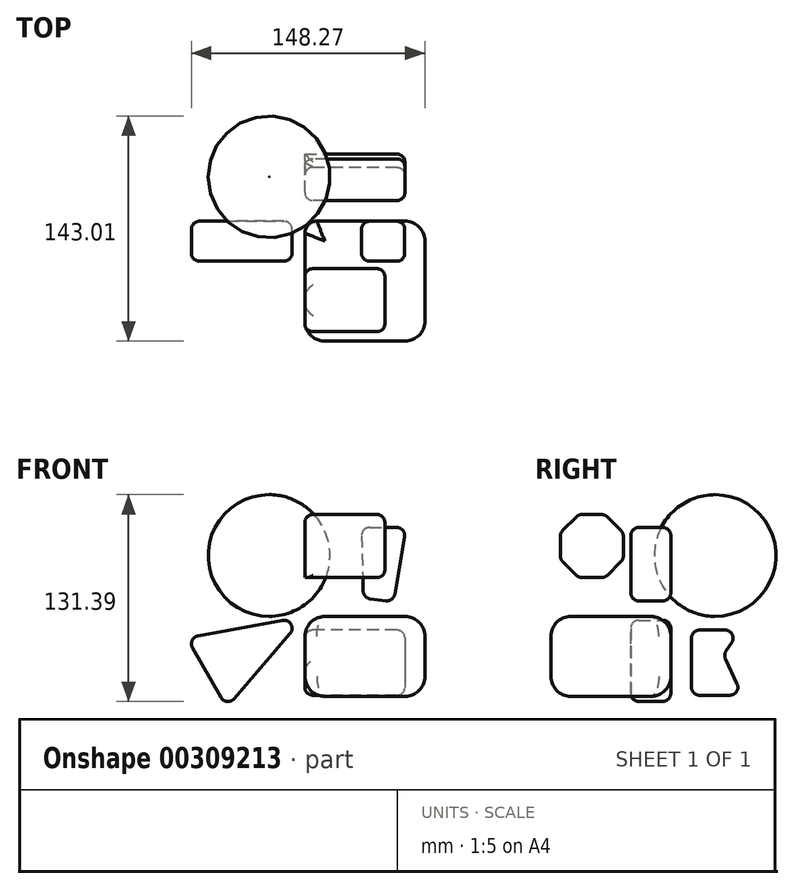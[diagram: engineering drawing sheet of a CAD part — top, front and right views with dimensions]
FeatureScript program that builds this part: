
annotation { "Feature Type Name" : "Feature", "Feature Type Description" : "" }
export const myFeature = defineFeature(function(context is Context, id is Id, definition is map)
    precondition{}
    {
        {
            var Q0;
            Q0=qCreatedBy(makeId("Top.planeOp"),FACE);
            var sketch = newSketch(context, id + "F0", { "sketchPlane" : qUnion([Q0])});
            skCircle(sketch, "E0", {"center": v(-22.77, 28.16) * mm, "radius": 38.66 * mm});
            skSolve(sketch);
        }
        {
            var Q0;
            Q0 = qSketchRegion(id + "F0", true);
            extrude(context, id + "F1", {"entities" : qUnion([Q0]), "depth" : 77.32 * mm});
        }
        {
            var Q0;
            Q0=makeQuery(id+"F1.opExtrude","CAP_EDGE",EDGE,{"disambiguationData":[OSD([sQuery(id+"F0.wireOp",EDGE,"E0")])],"isStart":false});
            var Q1;
            Q1=makeQuery(id+"F1.opExtrude","CAP_EDGE",EDGE,{"disambiguationData":[OSD([sQuery(id+"F0.wireOp",EDGE,"E0")])],"isStart":true});
            fillet(context, id + "F2", {"entities" : qUnion([Q0, Q1]), "radius" : 38.66 * mm, "tangentPropagation" : true, "allowEdgeOverflow" : false});
        }
        {
            var Q0;
            Q0=qCreatedBy(makeId("Front.planeOp"),FACE);
            var sketch = newSketch(context, id + "F3", { "sketchPlane" : qUnion([Q0])});
            skLineSegment(sketch, "E1", {"start": v(0, 0) * mm, "end": v(0, -50.8) * mm});
            skLineSegment(sketch, "E2", {"start": v(0, -50.8) * mm, "end": v(76.2, -50.8) * mm});
            skLineSegment(sketch, "E3", {"start": v(0, 0) * mm, "end": v(76.2, 0) * mm});
            skLineSegment(sketch, "E4", {"start": v(76.2, 0) * mm, "end": v(76.2, -50.8) * mm});
            skSolve(sketch);
        }
        {
            var Q0;
            Q0=makeQuery(id+"F3.imprint","IMPRINT",FACE,{"disambiguationData":[TD([[makeQuery(id+"F3.imprint","IMPRINT",EDGE,{"derivedFrom":sQuery(id+"F3.wireOp",EDGE,"E1")}),1.0]])]});
            extrude(context, id + "F4", {"entities" : qUnion([Q0]), "depth" : 76.2 * mm});
        }
        {
            var Q0;
            Q0=makeQuery(id+"F4.opExtrude","SWEPT_FACE",FACE,{"disambiguationData":[OSD([sQuery(id+"F3.wireOp",EDGE,"E4")])]});
            var Q1;
            Q1=makeQuery(id+"F4.opExtrude","CAP_FACE",FACE,{"disambiguationData":[OSD([sQuery(id+"F3.wireOp",EDGE,"E1"),sQuery(id+"F3.wireOp",EDGE,"E2"),sQuery(id+"F3.wireOp",EDGE,"E3"),sQuery(id+"F3.wireOp",EDGE,"E4")])],"isStart":false});
            var Q2;
            Q2=makeQuery(id+"F4.opExtrude","SWEPT_EDGE",EDGE,{"disambiguationData":[OSD([sQuery(id+"F3.wireOp",EDGE,"E1"),sQuery(id+"F3.wireOp",EDGE,"E3")])]});
            var Q3;
            Q3=makeQuery(id+"F4.opExtrude","CAP_EDGE",EDGE,{"disambiguationData":[OSD([sQuery(id+"F3.wireOp",EDGE,"E3")])],"isStart":true});
            var Q4;
            Q4=makeQuery(id+"F4.opExtrude","CAP_EDGE",EDGE,{"disambiguationData":[OSD([sQuery(id+"F3.wireOp",EDGE,"E2")])],"isStart":true});
            var Q5;
            Q5=makeQuery(id+"F4.opExtrude","SWEPT_EDGE",EDGE,{"disambiguationData":[OSD([sQuery(id+"F3.wireOp",EDGE,"E1"),sQuery(id+"F3.wireOp",EDGE,"E2")])]});
            fillet(context, id + "F5", {"entities" : qUnion([Q0, Q1, Q2, Q3, Q4, Q5]), "radius" : 12.7 * mm, "tangentPropagation" : true, "allowEdgeOverflow" : false});
        }
        {
            var Q0;
            Q0=makeQuery(id+"F4.opExtrude","CAP_EDGE",EDGE,{"disambiguationData":[OSD([sQuery(id+"F3.wireOp",EDGE,"E1")])],"isStart":true});
            fillet(context, id + "F6", {"entities" : qUnion([Q0]), "radius" : 7.62 * mm, "tangentPropagation" : true, "allowEdgeOverflow" : false});
        }
        {
            var Q0;
            Q0=qCreatedBy(makeId("Front.planeOp"),FACE);
            var sketch = newSketch(context, id + "F7", { "sketchPlane" : qUnion([Q0])});
            skLineSegment(sketch, "E5", {"start": v(0, 0) * mm, "end": v(-49.72, -57.75) * mm});
            skLineSegment(sketch, "E6", {"start": v(-49.72, -57.75) * mm, "end": v(-74.96, -13.67) * mm});
            skLineSegment(sketch, "E7", {"start": v(-74.96, -13.67) * mm, "end": v(0, 0) * mm});
            skSolve(sketch);
        }
        {
            var Q0;
            Q0=makeQuery(id+"F7.imprint","IMPRINT",FACE,{"disambiguationData":[TD([[makeQuery(id+"F7.imprint","IMPRINT",EDGE,{"derivedFrom":sQuery(id+"F7.wireOp",EDGE,"E5")}),-1.0]])]});
            extrude(context, id + "F8", {"entities" : qUnion([Q0]), "depth" : 25.4 * mm});
        }
        {
            var Q0;
            Q0=makeQuery(id+"F8.opExtrude","CAP_EDGE",EDGE,{"disambiguationData":[OSD([sQuery(id+"F7.wireOp",EDGE,"E7")])],"isStart":false});
            var Q1;
            Q1=makeQuery(id+"F8.opExtrude","CAP_EDGE",EDGE,{"disambiguationData":[OSD([sQuery(id+"F7.wireOp",EDGE,"E6")])],"isStart":false});
            var Q2;
            Q2=makeQuery(id+"F8.opExtrude","CAP_EDGE",EDGE,{"disambiguationData":[OSD([sQuery(id+"F7.wireOp",EDGE,"E5")])],"isStart":false});
            var Q3;
            Q3=makeQuery(id+"F8.opExtrude","CAP_EDGE",EDGE,{"disambiguationData":[OSD([sQuery(id+"F7.wireOp",EDGE,"E5")])],"isStart":true});
            var Q4;
            Q4=makeQuery(id+"F8.opExtrude","CAP_EDGE",EDGE,{"disambiguationData":[OSD([sQuery(id+"F7.wireOp",EDGE,"E6")])],"isStart":true});
            var Q5;
            Q5=makeQuery(id+"F8.opExtrude","SWEPT_EDGE",EDGE,{"disambiguationData":[OSD([sQuery(id+"F7.wireOp",EDGE,"E5"),sQuery(id+"F7.wireOp",EDGE,"E6")])]});
            var Q6;
            Q6=makeQuery(id+"F8.opExtrude","SWEPT_EDGE",EDGE,{"disambiguationData":[OSD([sQuery(id+"F7.wireOp",EDGE,"E6"),sQuery(id+"F7.wireOp",EDGE,"E7")])]});
            var Q7;
            Q7=makeQuery(id+"F8.opExtrude","CAP_EDGE",EDGE,{"disambiguationData":[OSD([sQuery(id+"F7.wireOp",EDGE,"E7")])],"isStart":true});
            var Q8;
            Q8=makeQuery(id+"F8.opExtrude","SWEPT_EDGE",EDGE,{"disambiguationData":[OSD([sQuery(id+"F7.wireOp",EDGE,"E5"),sQuery(id+"F7.wireOp",EDGE,"E7")])]});
            fillet(context, id + "F9", {"entities" : qUnion([Q0, Q1, Q2, Q3, Q4, Q5, Q6, Q7, Q8]), "radius" : 5.08 * mm, "tangentPropagation" : true, "allowEdgeOverflow" : false});
        }
        {
            var Q0;
            Q0=qCreatedBy(makeId("Right.planeOp"),FACE);
            var sketch = newSketch(context, id + "F10", { "sketchPlane" : qUnion([Q0])});
            skLineSegment(sketch, "E8", {"start": v(13.1, -8.7) * mm, "end": v(13.1, -50.08) * mm});
            skLineSegment(sketch, "E9", {"start": v(13.1, -8.7) * mm, "end": v(44, -8.7) * mm});
            skLineSegment(sketch, "E10", {"start": v(44, -8.7) * mm, "end": v(33.51, -24.43) * mm});
            skLineSegment(sketch, "E11", {"start": v(13.1, -50.08) * mm, "end": v(45.5, -50.08) * mm});
            skLineSegment(sketch, "E12", {"start": v(33.51, -24.43) * mm, "end": v(45.5, -50.08) * mm});
            skSolve(sketch);
        }
        {
            var Q0;
            Q0=makeQuery(id+"F10.imprint","IMPRINT",FACE,{"disambiguationData":[TD([[makeQuery(id+"F10.imprint","IMPRINT",EDGE,{"derivedFrom":sQuery(id+"F10.wireOp",EDGE,"E8")}),1.0]])]});
            extrude(context, id + "F11", {"entities" : qUnion([Q0]), "depth" : 63.5 * mm});
        }
        {
            var Q0;
            Q0=makeQuery(id+"F11.opExtrude","CAP_EDGE",EDGE,{"disambiguationData":[OSD([sQuery(id+"F10.wireOp",EDGE,"E9")])],"isStart":false});
            var Q1;
            Q1=makeQuery(id+"F11.opExtrude","CAP_EDGE",EDGE,{"disambiguationData":[OSD([sQuery(id+"F10.wireOp",EDGE,"E8")])],"isStart":false});
            var Q2;
            Q2=makeQuery(id+"F11.opExtrude","CAP_EDGE",EDGE,{"disambiguationData":[OSD([sQuery(id+"F10.wireOp",EDGE,"E11")])],"isStart":false});
            var Q3;
            Q3=makeQuery(id+"F11.opExtrude","CAP_EDGE",EDGE,{"disambiguationData":[OSD([sQuery(id+"F10.wireOp",EDGE,"E12")])],"isStart":false});
            var Q4;
            Q4=makeQuery(id+"F11.opExtrude","CAP_EDGE",EDGE,{"disambiguationData":[OSD([sQuery(id+"F10.wireOp",EDGE,"E10")])],"isStart":false});
            var Q5;
            Q5=makeQuery(id+"F11.opExtrude","SWEPT_EDGE",EDGE,{"disambiguationData":[OSD([sQuery(id+"F10.wireOp",EDGE,"E9"),sQuery(id+"F10.wireOp",EDGE,"E10")])]});
            var Q6;
            Q6=makeQuery(id+"F11.opExtrude","SWEPT_FACE",FACE,{"disambiguationData":[OSD([sQuery(id+"F10.wireOp",EDGE,"E10")])]});
            var Q7;
            Q7=makeQuery(id+"F11.opExtrude","SWEPT_EDGE",EDGE,{"disambiguationData":[OSD([sQuery(id+"F10.wireOp",EDGE,"E11"),sQuery(id+"F10.wireOp",EDGE,"E12")])]});
            var Q8;
            Q8=makeQuery(id+"F11.opExtrude","SWEPT_FACE",FACE,{"disambiguationData":[OSD([sQuery(id+"F10.wireOp",EDGE,"E9")])]});
            var Q9;
            Q9=makeQuery(id+"F11.opExtrude","CAP_EDGE",EDGE,{"disambiguationData":[OSD([sQuery(id+"F10.wireOp",EDGE,"E8")])],"isStart":true});
            var Q10;
            Q10=makeQuery(id+"F11.opExtrude","SWEPT_EDGE",EDGE,{"disambiguationData":[OSD([sQuery(id+"F10.wireOp",EDGE,"E8"),sQuery(id+"F10.wireOp",EDGE,"E11")])]});
            var Q11;
            Q11=makeQuery(id+"F11.opExtrude","CAP_EDGE",EDGE,{"disambiguationData":[OSD([sQuery(id+"F10.wireOp",EDGE,"E11")])],"isStart":true});
            fillet(context, id + "F12", {"entities" : qUnion([Q0, Q1, Q2, Q3, Q4, Q5, Q6, Q7, Q8, Q9, Q10, Q11]), "radius" : 5.08 * mm, "tangentPropagation" : true, "allowEdgeOverflow" : false});
        }
        {
            var Q0;
            Q0=qCreatedBy(makeId("Front.planeOp"),FACE);
            var sketch = newSketch(context, id + "F13", { "sketchPlane" : qUnion([Q0])});
            skLineSegment(sketch, "E13", {"start": v(35.85, 56.44) * mm, "end": v(37.16, 11.7) * mm});
            skLineSegment(sketch, "E14", {"start": v(37.16, 11.7) * mm, "end": v(56.26, 9.26) * mm});
            skLineSegment(sketch, "E15", {"start": v(56.26, 9.26) * mm, "end": v(64.3, 56.44) * mm});
            skLineSegment(sketch, "E16", {"start": v(35.85, 56.44) * mm, "end": v(64.3, 56.44) * mm});
            skSolve(sketch);
        }
        {
            var Q0;
            Q0 = qSketchRegion(id + "F13", true);
            extrude(context, id + "F14", {"entities" : qUnion([Q0]), "depth" : 25.4 * mm});
        }
        {
            var Q0;
            Q0=makeQuery(id+"F14.opExtrude","CAP_FACE",FACE,{"disambiguationData":[OSD([sQuery(id+"F13.wireOp",EDGE,"E13"),sQuery(id+"F13.wireOp",EDGE,"E14"),sQuery(id+"F13.wireOp",EDGE,"E15"),sQuery(id+"F13.wireOp",EDGE,"E16")])],"isStart":false});
            var Q1;
            Q1=makeQuery(id+"F14.opExtrude","SWEPT_FACE",FACE,{"disambiguationData":[OSD([sQuery(id+"F13.wireOp",EDGE,"E16")])]});
            var Q2;
            Q2=makeQuery(id+"F14.opExtrude","SWEPT_FACE",FACE,{"disambiguationData":[OSD([sQuery(id+"F13.wireOp",EDGE,"E15")])]});
            var Q3;
            Q3=makeQuery(id+"F14.opExtrude","CAP_FACE",FACE,{"disambiguationData":[OSD([sQuery(id+"F13.wireOp",EDGE,"E13"),sQuery(id+"F13.wireOp",EDGE,"E14"),sQuery(id+"F13.wireOp",EDGE,"E15"),sQuery(id+"F13.wireOp",EDGE,"E16")])],"isStart":true});
            var Q4;
            Q4=makeQuery(id+"F14.opExtrude","SWEPT_EDGE",EDGE,{"disambiguationData":[OSD([sQuery(id+"F13.wireOp",EDGE,"E13"),sQuery(id+"F13.wireOp",EDGE,"E14")])]});
            fillet(context, id + "F15", {"entities" : qUnion([Q0, Q1, Q2, Q3, Q4]), "radius" : 5.08 * mm, "tangentPropagation" : true, "allowEdgeOverflow" : false});
        }
        {
            var Q0;
            Q0=qCreatedBy(makeId("Right.planeOp"),FACE);
            var sketch = newSketch(context, id + "F16", { "sketchPlane" : qUnion([Q0])});
            skCircle(sketch, "E17.cCircle", {"center": v(-50.17, 44.65) * mm, "radius": 20.03 * mm, "construction": true});
            skLineSegment(sketch, "E17.0", {"start": v(-41.88, 24.62) * mm, "end": v(-58.47, 24.62) * mm});
            skLineSegment(sketch, "E17.1", {"start": v(-58.47, 24.62) * mm, "end": v(-70.2, 36.35) * mm});
            skLineSegment(sketch, "E17.2", {"start": v(-70.2, 36.35) * mm, "end": v(-70.2, 52.95) * mm});
            skLineSegment(sketch, "E17.3", {"start": v(-70.2, 52.95) * mm, "end": v(-58.47, 64.68) * mm});
            skLineSegment(sketch, "E17.4", {"start": v(-58.47, 64.68) * mm, "end": v(-41.88, 64.68) * mm});
            skLineSegment(sketch, "E17.5", {"start": v(-41.88, 64.68) * mm, "end": v(-30.14, 52.95) * mm});
            skLineSegment(sketch, "E17.6", {"start": v(-30.14, 52.95) * mm, "end": v(-30.14, 36.35) * mm});
            skLineSegment(sketch, "E17.7", {"start": v(-30.14, 36.35) * mm, "end": v(-41.88, 24.62) * mm});
            skPoint(sketch, "E17.0.midPoint", {"position": v(-50.17, 24.62) * mm});
            skSolve(sketch);
        }
        {
            var Q0;
            Q0=makeQuery(id+"F16.imprint","IMPRINT",FACE,{"disambiguationData":[TD([[makeQuery(id+"F16.imprint","IMPRINT",EDGE,{"derivedFrom":sQuery(id+"F16.wireOp",EDGE,"E17.0")}),-1.0]])]});
            extrude(context, id + "F17", {"entities" : qUnion([Q0]), "depth" : 50.8 * mm});
        }
        {
            var Q0;
            Q0=makeQuery(id+"F17.opExtrude","SWEPT_FACE",FACE,{"disambiguationData":[OSD([sQuery(id+"F16.wireOp",EDGE,"E17.3")])]});
            var Q1;
            Q1=makeQuery(id+"F17.opExtrude","SWEPT_FACE",FACE,{"disambiguationData":[OSD([sQuery(id+"F16.wireOp",EDGE,"E17.2")])]});
            var Q2;
            Q2=makeQuery(id+"F17.opExtrude","SWEPT_FACE",FACE,{"disambiguationData":[OSD([sQuery(id+"F16.wireOp",EDGE,"E17.1")])]});
            var Q3;
            Q3=makeQuery(id+"F17.opExtrude","CAP_FACE",FACE,{"disambiguationData":[OSD([sQuery(id+"F16.wireOp",EDGE,"E17.0"),sQuery(id+"F16.wireOp",EDGE,"E17.1"),sQuery(id+"F16.wireOp",EDGE,"E17.2"),sQuery(id+"F16.wireOp",EDGE,"E17.3"),sQuery(id+"F16.wireOp",EDGE,"E17.4"),sQuery(id+"F16.wireOp",EDGE,"E17.5"),sQuery(id+"F16.wireOp",EDGE,"E17.6"),sQuery(id+"F16.wireOp",EDGE,"E17.7")])],"isStart":false});
            var Q4;
            Q4=makeQuery(id+"F17.opExtrude","SWEPT_FACE",FACE,{"disambiguationData":[OSD([sQuery(id+"F16.wireOp",EDGE,"E17.4")])]});
            var Q5;
            Q5=makeQuery(id+"F17.opExtrude","SWEPT_FACE",FACE,{"disambiguationData":[OSD([sQuery(id+"F16.wireOp",EDGE,"E17.5")])]});
            var Q6;
            Q6=makeQuery(id+"F17.opExtrude","SWEPT_FACE",FACE,{"disambiguationData":[OSD([sQuery(id+"F16.wireOp",EDGE,"E17.6")])]});
            var Q7;
            Q7=makeQuery(id+"F17.opExtrude","SWEPT_FACE",FACE,{"disambiguationData":[OSD([sQuery(id+"F16.wireOp",EDGE,"E17.7")])]});
            fillet(context, id + "F18", {"entities" : qUnion([Q0, Q1, Q2, Q3, Q4, Q5, Q6, Q7]), "radius" : 5.08 * mm, "tangentPropagation" : true, "allowEdgeOverflow" : false});
        }
    });
